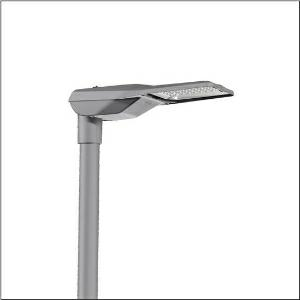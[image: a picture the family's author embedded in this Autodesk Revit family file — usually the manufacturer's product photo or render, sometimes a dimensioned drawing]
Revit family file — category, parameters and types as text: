
# Revit family: streetlight_sl_21_mini___p1_0a_5xe2a33s08gb_ad59
name_source: partatom
category: Lighting Fixtures
units: mm (PartAtom-declared; Revit-internal decimal feet)

## family parameters
Cut with Voids When Loaded = No
Host = Face
Light Source = No
Part Type = Normal
Room Calculation Point = No
Round Connector Dimension = Use Diameter
Shared = No

## types (1)
- --- (1 x LED, 5940 lm, 40.4 W, 3000K)
    Apparent Load = 40 VA
    CIE Flux Codes = 21 50 90 100 100
    Color Rendering = 70
    Color Temperature = 3000K
    Default Elevation = 1800 mm
    Description = Streetlight SL 21 mini, mast luminaire, primary light control with lens, of PMMA, primary optical cover: cover, of toughened safety glass, transparent, light distribution: P1.0a, light emission: direct distribution, primary light characteristic: asymmetric, installation type: side-entry, post-top, LED, High Power LED, rated luminous flux: 5.940lm, luminous efficacy: 147lm/W, light colour: 730, colour temperature: 3000K, control gear: D4i, control: overheat protection, constant luminous flux control, time-dependent luminous flux control, flexible luminous flux parameterisation, pre-setting: logarithmic dimming characteristic, mains connection: 220..240V, AC, 50/60Hz, start of lifetime: 40W, end of service life: 41W, reduction: 19W, luminaire housing, of diecast aluminium, powder-coated, Siteco® metallic grey (DB 702S), corrosivity category C5 mid according to DIN EN ISO 12944, please order mast flange separately, inclination adjustable: 0°, 5°, 10°, 15°, sealing non-destructively replaceable, multi-level sealing system, length: 628mm, width: 235mm, height: 110mm, mast flange for spigot size: 42mm (side-entry): 5XC10008XM4, 60/48mm (side-entry/post-top): 5XC10108XM2, 76/60mm (side-entry/post-top): 5XC10108XM1, mounting height: 4..8m, Smart Interface above, protection rating (complete): IP66, insulation class (complete): insulation class II (safety insulation), certification: CE, ENEC, ENEC+, VDE, impact resistance: IK10, permissible operating ambient temperature for outdoor applications: -40..+50°C, standard-compliant lighting for roads and squares, packaging unit: 1 piece

Light Distribution: P1.0a
    Height = 110 mm
    Lamp = 1 x LED
    Lamp Light Flux = 5940 lm
    Lamp Power = 40.4 W
    Lamp count = 1
    Length = 625 mm
    Luminous efficacy = 147 lm/W
    Manufacturer = Siteco
    ModVariant = No
    Model = 5XE2A33S08GB
    Number of Poles = 1
    OnlyDefault = Yes
    Power Factor = 1
    Product Name = Streetlight SL 21 mini | P1.0a
    Product group = mast luminaire | pylon top
    ProductGroupID = 6100
    Protection Class = Protection class II
    Protection Degree = IP 66
    RLX_Detail_Level = 1
    RLX_Emergency_Light_Flux = 0 lm
    RLX_Emergency_Type = 0
    RLX_Emergency_Type_DB = No
    RlxData = <blob elided: 37397 chars, md5=22edfdf7>
    Socket = socket
    Standby Power = 0 W
    System Light Flux = 5940 lm
    System Power = 40 W
    Type Comments = factory setting: luminous flux: 100 % | dim-lin: 254 | 812 mA
    Type Image = l_1003515.jpg
    URL = http://relux.com
    VarID = @adj_186700
    Voltage = 0 V
    Weight = 0.00 kg
    Width = 234 mm

## geometry (parser evidence)
native form markers: Blend x4, Sweep x10
no freeform markers — native parametric forms only
